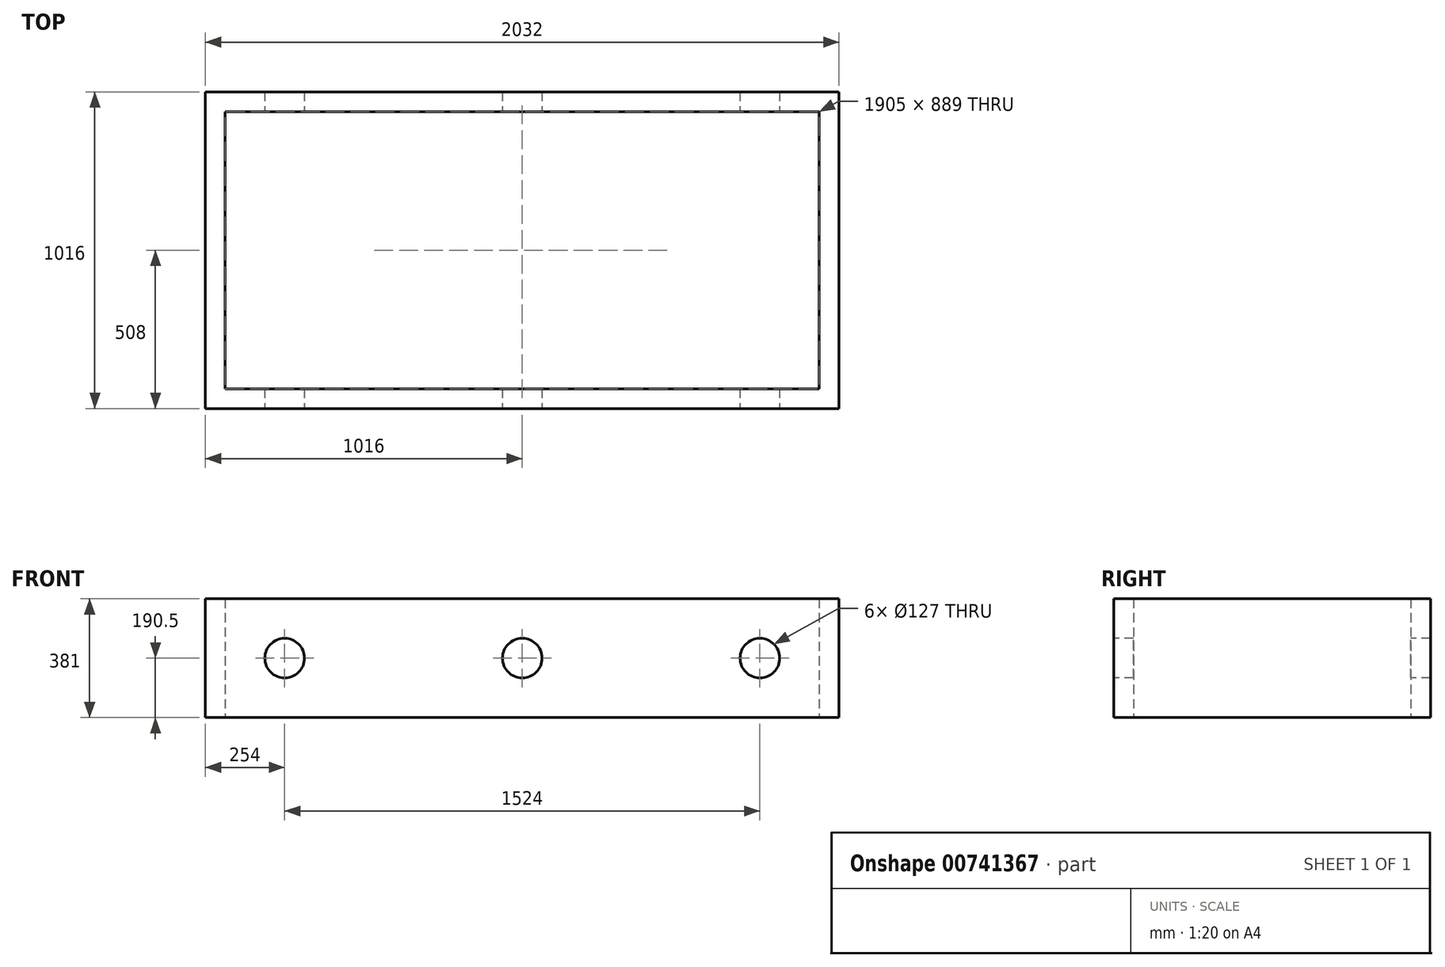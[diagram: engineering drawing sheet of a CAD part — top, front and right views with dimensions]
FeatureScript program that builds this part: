
annotation { "Feature Type Name" : "Feature", "Feature Type Description" : "" }
export const myFeature = defineFeature(function(context is Context, id is Id, definition is map)
    precondition{}
    {
        {
            var Q0;
            Q0=qCreatedBy(makeId("Top.planeOp"),FACE);
            var sketch = newSketch(context, id + "F0", { "sketchPlane" : qUnion([Q0])});
            skLineSegment(sketch, "E0.bottom", {"start": v(1016, 508) * mm, "end": v(-1016, 508) * mm});
            skLineSegment(sketch, "E0.top", {"start": v(1016, -508) * mm, "end": v(-1016, -508) * mm});
            skLineSegment(sketch, "E0.left", {"start": v(1016, 508) * mm, "end": v(1016, -508) * mm});
            skLineSegment(sketch, "E0.right", {"start": v(-1016, 508) * mm, "end": v(-1016, -508) * mm});
            skPoint(sketch, "E0.middle", {"position": v(0, 0) * mm});
            skLineSegment(sketch, "E1.bottom", {"start": v(952.5, 444.5) * mm, "end": v(-952.5, 444.5) * mm});
            skLineSegment(sketch, "E1.top", {"start": v(952.5, -444.5) * mm, "end": v(-952.5, -444.5) * mm});
            skLineSegment(sketch, "E1.left", {"start": v(952.5, 444.5) * mm, "end": v(952.5, -444.5) * mm});
            skLineSegment(sketch, "E1.right", {"start": v(-952.5, 444.5) * mm, "end": v(-952.5, -444.5) * mm});
            skSolve(sketch);
        }
        {
            var Q0;
            Q0 = qSketchRegion(id + "F0", true);
            extrude(context, id + "F1", {"entities" : qUnion([Q0]), "endBound" : BoundingType.SYMMETRIC, "depth" : 381 * mm, "offsetDistance" : 25.4 * mm});
        }
        {
            var Q0;
            Q0=makeQuery(id+"F1.opExtrude","SWEPT_FACE",FACE,{"disambiguationData":[OSD([sQuery(id+"F0.wireOp",EDGE,"E0.top")])]});
            var sketch = newSketch(context, id + "F2", { "sketchPlane" : qUnion([Q0])});
            skLineSegment(sketch, "E2", {"start": v(-762, 0) * mm, "end": v(762, 0) * mm});
            skCircle(sketch, "E3", {"center": v(0, 0) * mm, "radius": 63.5 * mm});
            skCircle(sketch, "E4", {"center": v(762, 0) * mm, "radius": 63.5 * mm});
            skCircle(sketch, "E5", {"center": v(-762, 0) * mm, "radius": 63.5 * mm});
            skSolve(sketch);
        }
        {
            var Q0;
            Q0 = qSketchRegion(id + "F2", true);
            extrude(context, id + "F3", {"entities" : qUnion([Q0]), "operationType" : NewBodyOperationType.REMOVE, "endBound" : BoundingType.THROUGH_ALL, "oppositeDirection" : true, "depth" : 25.4 * mm, "offsetDistance" : 25.4 * mm});
        }
    });
